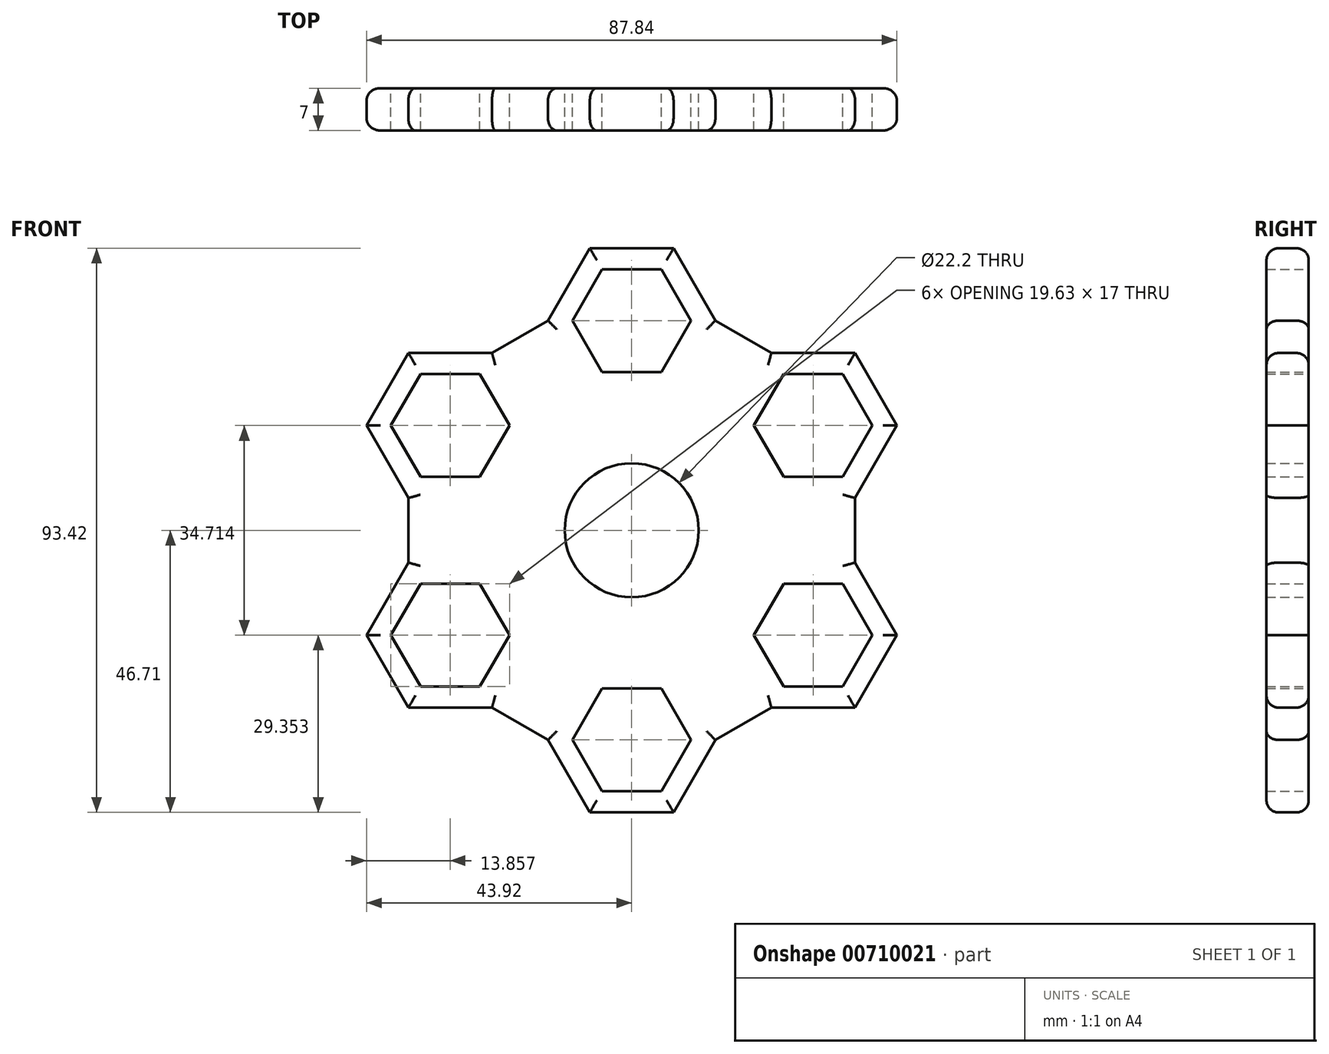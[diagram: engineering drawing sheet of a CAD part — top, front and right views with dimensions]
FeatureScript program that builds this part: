
annotation { "Feature Type Name" : "Feature", "Feature Type Description" : "" }
export const myFeature = defineFeature(function(context is Context, id is Id, definition is map)
    precondition{}
    {
        {
            var Q0;
            Q0=qCreatedBy(makeId("Front.planeOp"),FACE);
            var sketch = newSketch(context, id + "F0", { "sketchPlane" : qUnion([Q0])});
            skCircle(sketch, "E0", {"center": v(0, 0) * mm, "radius": 14.5 * mm});
            skCircle(sketch, "E1", {"center": v(0, 0) * mm, "radius": 11.1 * mm});
            skCircle(sketch, "E2.cCircle", {"center": v(0, 34.71) * mm, "radius": 8.5 * mm, "construction": true});
            skLineSegment(sketch, "E2.0", {"start": v(4.9, 26.21) * mm, "end": v(-4.9, 26.21) * mm});
            skLineSegment(sketch, "E2.1", {"start": v(-4.9, 26.21) * mm, "end": v(-9.81, 34.71) * mm});
            skLineSegment(sketch, "E2.2", {"start": v(-9.81, 34.71) * mm, "end": v(-4.9, 43.21) * mm});
            skLineSegment(sketch, "E2.3", {"start": v(-4.9, 43.21) * mm, "end": v(4.9, 43.21) * mm});
            skLineSegment(sketch, "E2.4", {"start": v(4.9, 43.21) * mm, "end": v(9.81, 34.71) * mm});
            skLineSegment(sketch, "E2.5", {"start": v(9.81, 34.71) * mm, "end": v(4.9, 26.21) * mm});
            skPoint(sketch, "E2.0.midPoint", {"position": v(0, 26.21) * mm});
            skCircle(sketch, "E3.cCircle", {"center": v(0, 34.71) * mm, "radius": 12 * mm, "construction": true});
            skLineSegment(sketch, "E3.0", {"start": v(6.93, 22.71) * mm, "end": v(-6.93, 22.71) * mm});
            skLineSegment(sketch, "E3.1", {"start": v(-6.93, 22.71) * mm, "end": v(-13.86, 34.71) * mm});
            skLineSegment(sketch, "E3.2", {"start": v(-13.86, 34.71) * mm, "end": v(-6.93, 46.71) * mm});
            skLineSegment(sketch, "E3.3", {"start": v(-6.93, 46.71) * mm, "end": v(6.93, 46.71) * mm});
            skLineSegment(sketch, "E3.4", {"start": v(6.93, 46.71) * mm, "end": v(13.86, 34.71) * mm});
            skLineSegment(sketch, "E3.5", {"start": v(13.86, 34.71) * mm, "end": v(6.93, 22.71) * mm});
            skPoint(sketch, "E3.0.midPoint", {"position": v(0, 22.71) * mm});
            skCircle(sketch, "E4.1.1", {"center": v(-30.06, 17.36) * mm, "radius": 12 * mm, "construction": true});
            skLineSegment(sketch, "E4.1.2", {"start": v(-23.14, 5.36) * mm, "end": v(-37, 5.36) * mm});
            skLineSegment(sketch, "E4.1.3", {"start": v(-37, 5.36) * mm, "end": v(-43.92, 17.36) * mm});
            skPoint(sketch, "E4.1.4", {"position": v(-22.7, 13.1) * mm});
            skLineSegment(sketch, "E4.1.6", {"start": v(-23.14, 29.36) * mm, "end": v(-16.2, 17.36) * mm});
            skLineSegment(sketch, "E4.1.7", {"start": v(-37, 29.36) * mm, "end": v(-23.14, 29.36) * mm});
            skLineSegment(sketch, "E4.1.8", {"start": v(-43.92, 17.36) * mm, "end": v(-37, 29.36) * mm});
            skPoint(sketch, "E4.1.9", {"position": v(-19.67, 11.36) * mm});
            skCircle(sketch, "E4.1.10", {"center": v(-30.06, 17.36) * mm, "radius": 8.5 * mm, "construction": true});
            skLineSegment(sketch, "E4.1.11", {"start": v(-16.2, 17.36) * mm, "end": v(-23.14, 5.36) * mm});
            skLineSegment(sketch, "E4.1.12", {"start": v(-25.16, 25.86) * mm, "end": v(-20.25, 17.36) * mm});
            skLineSegment(sketch, "E4.1.13", {"start": v(-34.97, 25.86) * mm, "end": v(-25.16, 25.86) * mm});
            skLineSegment(sketch, "E4.1.14", {"start": v(-39.88, 17.36) * mm, "end": v(-34.97, 25.86) * mm});
            skLineSegment(sketch, "E4.1.15", {"start": v(-20.25, 17.36) * mm, "end": v(-25.16, 8.86) * mm});
            skLineSegment(sketch, "E4.1.16", {"start": v(-25.16, 8.86) * mm, "end": v(-34.97, 8.86) * mm});
            skLineSegment(sketch, "E4.1.17", {"start": v(-34.97, 8.86) * mm, "end": v(-39.88, 17.36) * mm});
            skCircle(sketch, "E4.2.1", {"center": v(-30.06, -17.36) * mm, "radius": 12 * mm, "construction": true});
            skLineSegment(sketch, "E4.2.2", {"start": v(-16.2, -17.36) * mm, "end": v(-23.14, -29.36) * mm});
            skLineSegment(sketch, "E4.2.3", {"start": v(-23.14, -29.36) * mm, "end": v(-37, -29.36) * mm});
            skPoint(sketch, "E4.2.4", {"position": v(-22.7, -13.1) * mm});
            skLineSegment(sketch, "E4.2.6", {"start": v(-37, -5.36) * mm, "end": v(-23.14, -5.36) * mm});
            skLineSegment(sketch, "E4.2.7", {"start": v(-43.92, -17.36) * mm, "end": v(-37, -5.36) * mm});
            skLineSegment(sketch, "E4.2.8", {"start": v(-37, -29.36) * mm, "end": v(-43.92, -17.36) * mm});
            skPoint(sketch, "E4.2.9", {"position": v(-19.67, -11.36) * mm});
            skCircle(sketch, "E4.2.10", {"center": v(-30.06, -17.36) * mm, "radius": 8.5 * mm, "construction": true});
            skLineSegment(sketch, "E4.2.11", {"start": v(-23.14, -5.36) * mm, "end": v(-16.2, -17.36) * mm});
            skLineSegment(sketch, "E4.2.12", {"start": v(-34.97, -8.86) * mm, "end": v(-25.16, -8.86) * mm});
            skLineSegment(sketch, "E4.2.13", {"start": v(-39.88, -17.36) * mm, "end": v(-34.97, -8.86) * mm});
            skLineSegment(sketch, "E4.2.14", {"start": v(-34.97, -25.86) * mm, "end": v(-39.88, -17.36) * mm});
            skLineSegment(sketch, "E4.2.15", {"start": v(-25.16, -8.86) * mm, "end": v(-20.25, -17.36) * mm});
            skLineSegment(sketch, "E4.2.16", {"start": v(-20.25, -17.36) * mm, "end": v(-25.16, -25.86) * mm});
            skLineSegment(sketch, "E4.2.17", {"start": v(-25.16, -25.86) * mm, "end": v(-34.97, -25.86) * mm});
            skCircle(sketch, "E4.3.1", {"center": v(0, -34.71) * mm, "radius": 12 * mm, "construction": true});
            skLineSegment(sketch, "E4.3.2", {"start": v(6.93, -22.71) * mm, "end": v(13.86, -34.71) * mm});
            skLineSegment(sketch, "E4.3.3", {"start": v(13.86, -34.71) * mm, "end": v(6.93, -46.71) * mm});
            skPoint(sketch, "E4.3.4", {"position": v(0, -26.21) * mm});
            skLineSegment(sketch, "E4.3.6", {"start": v(-13.86, -34.71) * mm, "end": v(-6.93, -22.71) * mm});
            skLineSegment(sketch, "E4.3.7", {"start": v(-6.93, -46.71) * mm, "end": v(-13.86, -34.71) * mm});
            skLineSegment(sketch, "E4.3.8", {"start": v(6.93, -46.71) * mm, "end": v(-6.93, -46.71) * mm});
            skPoint(sketch, "E4.3.9", {"position": v(0, -22.71) * mm});
            skCircle(sketch, "E4.3.10", {"center": v(0, -34.71) * mm, "radius": 8.5 * mm, "construction": true});
            skLineSegment(sketch, "E4.3.11", {"start": v(-6.93, -22.71) * mm, "end": v(6.93, -22.71) * mm});
            skLineSegment(sketch, "E4.3.12", {"start": v(-9.81, -34.71) * mm, "end": v(-4.9, -26.21) * mm});
            skLineSegment(sketch, "E4.3.13", {"start": v(-4.9, -43.21) * mm, "end": v(-9.81, -34.71) * mm});
            skLineSegment(sketch, "E4.3.14", {"start": v(4.9, -43.21) * mm, "end": v(-4.9, -43.21) * mm});
            skLineSegment(sketch, "E4.3.15", {"start": v(-4.9, -26.21) * mm, "end": v(4.9, -26.21) * mm});
            skLineSegment(sketch, "E4.3.16", {"start": v(4.9, -26.21) * mm, "end": v(9.81, -34.71) * mm});
            skLineSegment(sketch, "E4.3.17", {"start": v(9.81, -34.71) * mm, "end": v(4.9, -43.21) * mm});
            skCircle(sketch, "E4.4.1", {"center": v(30.06, -17.36) * mm, "radius": 12 * mm, "construction": true});
            skLineSegment(sketch, "E4.4.2", {"start": v(23.14, -5.36) * mm, "end": v(37, -5.36) * mm});
            skLineSegment(sketch, "E4.4.3", {"start": v(37, -5.36) * mm, "end": v(43.92, -17.36) * mm});
            skPoint(sketch, "E4.4.4", {"position": v(22.7, -13.1) * mm});
            skLineSegment(sketch, "E4.4.6", {"start": v(23.14, -29.36) * mm, "end": v(16.2, -17.36) * mm});
            skLineSegment(sketch, "E4.4.7", {"start": v(37, -29.36) * mm, "end": v(23.14, -29.36) * mm});
            skLineSegment(sketch, "E4.4.8", {"start": v(43.92, -17.36) * mm, "end": v(37, -29.36) * mm});
            skPoint(sketch, "E4.4.9", {"position": v(19.67, -11.36) * mm});
            skCircle(sketch, "E4.4.10", {"center": v(30.06, -17.36) * mm, "radius": 8.5 * mm, "construction": true});
            skLineSegment(sketch, "E4.4.11", {"start": v(16.2, -17.36) * mm, "end": v(23.14, -5.36) * mm});
            skLineSegment(sketch, "E4.4.12", {"start": v(25.16, -25.86) * mm, "end": v(20.25, -17.36) * mm});
            skLineSegment(sketch, "E4.4.13", {"start": v(34.97, -25.86) * mm, "end": v(25.16, -25.86) * mm});
            skLineSegment(sketch, "E4.4.14", {"start": v(39.88, -17.36) * mm, "end": v(34.97, -25.86) * mm});
            skLineSegment(sketch, "E4.4.15", {"start": v(20.25, -17.36) * mm, "end": v(25.16, -8.86) * mm});
            skLineSegment(sketch, "E4.4.16", {"start": v(25.16, -8.86) * mm, "end": v(34.97, -8.86) * mm});
            skLineSegment(sketch, "E4.4.17", {"start": v(34.97, -8.86) * mm, "end": v(39.88, -17.36) * mm});
            skCircle(sketch, "E4.5.1", {"center": v(30.06, 17.36) * mm, "radius": 12 * mm, "construction": true});
            skLineSegment(sketch, "E4.5.2", {"start": v(16.2, 17.36) * mm, "end": v(23.14, 29.36) * mm});
            skLineSegment(sketch, "E4.5.3", {"start": v(23.14, 29.36) * mm, "end": v(37, 29.36) * mm});
            skPoint(sketch, "E4.5.4", {"position": v(22.7, 13.1) * mm});
            skLineSegment(sketch, "E4.5.6", {"start": v(37, 5.36) * mm, "end": v(23.14, 5.36) * mm});
            skLineSegment(sketch, "E4.5.7", {"start": v(43.92, 17.36) * mm, "end": v(37, 5.36) * mm});
            skLineSegment(sketch, "E4.5.8", {"start": v(37, 29.36) * mm, "end": v(43.92, 17.36) * mm});
            skPoint(sketch, "E4.5.9", {"position": v(19.67, 11.36) * mm});
            skCircle(sketch, "E4.5.10", {"center": v(30.06, 17.36) * mm, "radius": 8.5 * mm, "construction": true});
            skLineSegment(sketch, "E4.5.11", {"start": v(23.14, 5.36) * mm, "end": v(16.2, 17.36) * mm});
            skLineSegment(sketch, "E4.5.12", {"start": v(34.97, 8.86) * mm, "end": v(25.16, 8.86) * mm});
            skLineSegment(sketch, "E4.5.13", {"start": v(39.88, 17.36) * mm, "end": v(34.97, 8.86) * mm});
            skLineSegment(sketch, "E4.5.14", {"start": v(34.97, 25.86) * mm, "end": v(39.88, 17.36) * mm});
            skLineSegment(sketch, "E4.5.15", {"start": v(25.16, 8.86) * mm, "end": v(20.25, 17.36) * mm});
            skLineSegment(sketch, "E4.5.16", {"start": v(20.25, 17.36) * mm, "end": v(25.16, 25.86) * mm});
            skLineSegment(sketch, "E4.5.17", {"start": v(25.16, 25.86) * mm, "end": v(34.97, 25.86) * mm});
            skLineSegment(sketch, "E5", {"start": v(13.86, 34.71) * mm, "end": v(23.14, 29.36) * mm});
            skLineSegment(sketch, "E6.1.0", {"start": v(-23.14, 29.36) * mm, "end": v(-13.86, 34.71) * mm});
            skLineSegment(sketch, "E6.2.0", {"start": v(-37, -5.36) * mm, "end": v(-37, 5.36) * mm});
            skLineSegment(sketch, "E6.3.0", {"start": v(-13.86, -34.71) * mm, "end": v(-23.14, -29.36) * mm});
            skLineSegment(sketch, "E6.4.0", {"start": v(23.14, -29.36) * mm, "end": v(13.86, -34.71) * mm});
            skLineSegment(sketch, "E6.5.0", {"start": v(37, 5.36) * mm, "end": v(37, -5.36) * mm});
            skSolve(sketch);
        }
        {
            var Q0;
            Q0=makeQuery(id+"F0.imprint","IMPRINT",FACE,{"disambiguationData":[TD([[makeQuery(id+"F0.imprint","IMPRINT",EDGE,{"derivedFrom":sQuery(id+"F0.wireOp",EDGE,"E4.1.2")}),-1.0]])]});
            var Q1;
            Q1=makeQuery(id+"F0.imprint","IMPRINT",FACE,{"disambiguationData":[TD([[makeQuery(id+"F0.imprint","IMPRINT",EDGE,{"derivedFrom":sQuery(id+"F0.wireOp",EDGE,"E2.0")}),1.0]])]});
            var Q2;
            Q2=makeQuery(id+"F0.imprint","IMPRINT",FACE,{"disambiguationData":[TD([[makeQuery(id+"F0.imprint","IMPRINT",EDGE,{"derivedFrom":sQuery(id+"F0.wireOp",EDGE,"E3.0")}),1.0]])]});
            var Q3;
            Q3=makeQuery(id+"F0.imprint","IMPRINT",FACE,{"disambiguationData":[TD([[makeQuery(id+"F0.imprint","IMPRINT",EDGE,{"derivedFrom":sQuery(id+"F0.wireOp",EDGE,"E1")}),-1.0]])]});
            var Q4;
            Q4=makeQuery(id+"F0.imprint","IMPRINT",FACE,{"disambiguationData":[TD([[makeQuery(id+"F0.imprint","IMPRINT",EDGE,{"derivedFrom":sQuery(id+"F0.wireOp",EDGE,"E4.2.2")}),-1.0]])]});
            var Q5;
            Q5=makeQuery(id+"F0.imprint","IMPRINT",FACE,{"disambiguationData":[TD([[makeQuery(id+"F0.imprint","IMPRINT",EDGE,{"derivedFrom":sQuery(id+"F0.wireOp",EDGE,"E4.3.2")}),-1.0]])]});
            var Q6;
            Q6=makeQuery(id+"F0.imprint","IMPRINT",FACE,{"disambiguationData":[TD([[makeQuery(id+"F0.imprint","IMPRINT",EDGE,{"derivedFrom":sQuery(id+"F0.wireOp",EDGE,"E4.4.2")}),-1.0]])]});
            var Q7;
            Q7=makeQuery(id+"F0.imprint","IMPRINT",FACE,{"disambiguationData":[TD([[makeQuery(id+"F0.imprint","IMPRINT",EDGE,{"derivedFrom":sQuery(id+"F0.wireOp",EDGE,"E4.5.2")}),-1.0]])]});
            extrude(context, id + "F1", {"entities" : qUnion([Q0, Q1, Q2, Q3, Q4, Q5, Q6, Q7]), "depth" : 7 * mm, "offsetDistance" : 25 * mm});
        }
        {
            var Q0;
            Q0=makeQuery(id+"F1.opExtrude","CAP_EDGE",EDGE,{"disambiguationData":[OSD([sQuery(id+"F0.wireOp",EDGE,"E3.3")])],"isStart":false});
            var Q1;
            Q1=makeQuery(id+"F1.opExtrude","CAP_EDGE",EDGE,{"disambiguationData":[OSD([sQuery(id+"F0.wireOp",EDGE,"E3.4")])],"isStart":false});
            var Q2;
            Q2=makeQuery(id+"F1.opExtrude","CAP_EDGE",EDGE,{"disambiguationData":[OSD([sQuery(id+"F0.wireOp",EDGE,"E5")])],"isStart":false});
            var Q3;
            Q3=makeQuery(id+"F1.opExtrude","CAP_EDGE",EDGE,{"disambiguationData":[OSD([sQuery(id+"F0.wireOp",EDGE,"E4.5.3")])],"isStart":false});
            var Q4;
            Q4=makeQuery(id+"F1.opExtrude","CAP_EDGE",EDGE,{"disambiguationData":[OSD([sQuery(id+"F0.wireOp",EDGE,"E4.5.8")])],"isStart":false});
            var Q5;
            Q5=makeQuery(id+"F1.opExtrude","CAP_EDGE",EDGE,{"disambiguationData":[OSD([sQuery(id+"F0.wireOp",EDGE,"E4.5.7")])],"isStart":false});
            var Q6;
            Q6=makeQuery(id+"F1.opExtrude","CAP_EDGE",EDGE,{"disambiguationData":[OSD([sQuery(id+"F0.wireOp",EDGE,"E6.5.0")])],"isStart":false});
            var Q7;
            Q7=makeQuery(id+"F1.opExtrude","CAP_EDGE",EDGE,{"disambiguationData":[OSD([sQuery(id+"F0.wireOp",EDGE,"E4.4.3")])],"isStart":false});
            var Q8;
            Q8=makeQuery(id+"F1.opExtrude","CAP_EDGE",EDGE,{"disambiguationData":[OSD([sQuery(id+"F0.wireOp",EDGE,"E4.4.8")])],"isStart":false});
            var Q9;
            Q9=makeQuery(id+"F1.opExtrude","CAP_EDGE",EDGE,{"disambiguationData":[OSD([sQuery(id+"F0.wireOp",EDGE,"E3.2")])],"isStart":false});
            var Q10;
            Q10=makeQuery(id+"F1.opExtrude","CAP_EDGE",EDGE,{"disambiguationData":[OSD([sQuery(id+"F0.wireOp",EDGE,"E6.1.0")])],"isStart":false});
            var Q11;
            Q11=makeQuery(id+"F1.opExtrude","CAP_EDGE",EDGE,{"disambiguationData":[OSD([sQuery(id+"F0.wireOp",EDGE,"E4.1.7")])],"isStart":false});
            var Q12;
            Q12=makeQuery(id+"F1.opExtrude","CAP_EDGE",EDGE,{"disambiguationData":[OSD([sQuery(id+"F0.wireOp",EDGE,"E4.1.8")])],"isStart":false});
            var Q13;
            Q13=makeQuery(id+"F1.opExtrude","CAP_EDGE",EDGE,{"disambiguationData":[OSD([sQuery(id+"F0.wireOp",EDGE,"E4.1.3")])],"isStart":false});
            var Q14;
            Q14=makeQuery(id+"F1.opExtrude","CAP_EDGE",EDGE,{"disambiguationData":[OSD([sQuery(id+"F0.wireOp",EDGE,"E6.2.0")])],"isStart":false});
            var Q15;
            Q15=makeQuery(id+"F1.opExtrude","CAP_EDGE",EDGE,{"disambiguationData":[OSD([sQuery(id+"F0.wireOp",EDGE,"E4.2.7")])],"isStart":false});
            var Q16;
            Q16=makeQuery(id+"F1.opExtrude","CAP_EDGE",EDGE,{"disambiguationData":[OSD([sQuery(id+"F0.wireOp",EDGE,"E4.2.8")])],"isStart":false});
            var Q17;
            Q17=makeQuery(id+"F1.opExtrude","CAP_EDGE",EDGE,{"disambiguationData":[OSD([sQuery(id+"F0.wireOp",EDGE,"E6.3.0")])],"isStart":false});
            var Q18;
            Q18=makeQuery(id+"F1.opExtrude","CAP_EDGE",EDGE,{"disambiguationData":[OSD([sQuery(id+"F0.wireOp",EDGE,"E4.3.7")])],"isStart":false});
            var Q19;
            Q19=makeQuery(id+"F1.opExtrude","CAP_EDGE",EDGE,{"disambiguationData":[OSD([sQuery(id+"F0.wireOp",EDGE,"E4.3.8")])],"isStart":false});
            var Q20;
            Q20=makeQuery(id+"F1.opExtrude","CAP_EDGE",EDGE,{"disambiguationData":[OSD([sQuery(id+"F0.wireOp",EDGE,"E4.3.3")])],"isStart":false});
            var Q21;
            Q21=makeQuery(id+"F1.opExtrude","CAP_EDGE",EDGE,{"disambiguationData":[OSD([sQuery(id+"F0.wireOp",EDGE,"E6.4.0")])],"isStart":false});
            var Q22;
            Q22=makeQuery(id+"F1.opExtrude","CAP_EDGE",EDGE,{"disambiguationData":[OSD([sQuery(id+"F0.wireOp",EDGE,"E4.4.7")])],"isStart":false});
            var Q23;
            Q23=makeQuery(id+"F1.opExtrude","CAP_EDGE",EDGE,{"disambiguationData":[OSD([sQuery(id+"F0.wireOp",EDGE,"E4.2.3")])],"isStart":false});
            var Q24;
            Q24=makeQuery(id+"F1.opExtrude","CAP_EDGE",EDGE,{"disambiguationData":[OSD([sQuery(id+"F0.wireOp",EDGE,"E4.3.8")])],"isStart":true});
            var Q25;
            Q25=makeQuery(id+"F1.opExtrude","CAP_EDGE",EDGE,{"disambiguationData":[OSD([sQuery(id+"F0.wireOp",EDGE,"E4.3.3")])],"isStart":true});
            var Q26;
            Q26=makeQuery(id+"F1.opExtrude","CAP_EDGE",EDGE,{"disambiguationData":[OSD([sQuery(id+"F0.wireOp",EDGE,"E6.4.0")])],"isStart":true});
            var Q27;
            Q27=makeQuery(id+"F1.opExtrude","CAP_EDGE",EDGE,{"disambiguationData":[OSD([sQuery(id+"F0.wireOp",EDGE,"E4.4.7")])],"isStart":true});
            var Q28;
            Q28=makeQuery(id+"F1.opExtrude","CAP_EDGE",EDGE,{"disambiguationData":[OSD([sQuery(id+"F0.wireOp",EDGE,"E4.4.8")])],"isStart":true});
            var Q29;
            Q29=makeQuery(id+"F1.opExtrude","CAP_EDGE",EDGE,{"disambiguationData":[OSD([sQuery(id+"F0.wireOp",EDGE,"E4.4.3")])],"isStart":true});
            var Q30;
            Q30=makeQuery(id+"F1.opExtrude","CAP_EDGE",EDGE,{"disambiguationData":[OSD([sQuery(id+"F0.wireOp",EDGE,"E6.5.0")])],"isStart":true});
            var Q31;
            Q31=makeQuery(id+"F1.opExtrude","CAP_EDGE",EDGE,{"disambiguationData":[OSD([sQuery(id+"F0.wireOp",EDGE,"E4.5.7")])],"isStart":true});
            var Q32;
            Q32=makeQuery(id+"F1.opExtrude","CAP_EDGE",EDGE,{"disambiguationData":[OSD([sQuery(id+"F0.wireOp",EDGE,"E4.5.8")])],"isStart":true});
            var Q33;
            Q33=makeQuery(id+"F1.opExtrude","CAP_EDGE",EDGE,{"disambiguationData":[OSD([sQuery(id+"F0.wireOp",EDGE,"E4.5.3")])],"isStart":true});
            var Q34;
            Q34=makeQuery(id+"F1.opExtrude","CAP_EDGE",EDGE,{"disambiguationData":[OSD([sQuery(id+"F0.wireOp",EDGE,"E5")])],"isStart":true});
            var Q35;
            Q35=makeQuery(id+"F1.opExtrude","CAP_EDGE",EDGE,{"disambiguationData":[OSD([sQuery(id+"F0.wireOp",EDGE,"E3.4")])],"isStart":true});
            var Q36;
            Q36=makeQuery(id+"F1.opExtrude","CAP_EDGE",EDGE,{"disambiguationData":[OSD([sQuery(id+"F0.wireOp",EDGE,"E3.3")])],"isStart":true});
            var Q37;
            Q37=makeQuery(id+"F1.opExtrude","CAP_EDGE",EDGE,{"disambiguationData":[OSD([sQuery(id+"F0.wireOp",EDGE,"E3.2")])],"isStart":true});
            var Q38;
            Q38=makeQuery(id+"F1.opExtrude","CAP_EDGE",EDGE,{"disambiguationData":[OSD([sQuery(id+"F0.wireOp",EDGE,"E6.1.0")])],"isStart":true});
            var Q39;
            Q39=makeQuery(id+"F1.opExtrude","CAP_EDGE",EDGE,{"disambiguationData":[OSD([sQuery(id+"F0.wireOp",EDGE,"E4.1.7")])],"isStart":true});
            var Q40;
            Q40=makeQuery(id+"F1.opExtrude","CAP_EDGE",EDGE,{"disambiguationData":[OSD([sQuery(id+"F0.wireOp",EDGE,"E4.1.8")])],"isStart":true});
            var Q41;
            Q41=makeQuery(id+"F1.opExtrude","CAP_EDGE",EDGE,{"disambiguationData":[OSD([sQuery(id+"F0.wireOp",EDGE,"E4.1.3")])],"isStart":true});
            var Q42;
            Q42=makeQuery(id+"F1.opExtrude","CAP_EDGE",EDGE,{"disambiguationData":[OSD([sQuery(id+"F0.wireOp",EDGE,"E6.2.0")])],"isStart":true});
            var Q43;
            Q43=makeQuery(id+"F1.opExtrude","CAP_EDGE",EDGE,{"disambiguationData":[OSD([sQuery(id+"F0.wireOp",EDGE,"E4.2.7")])],"isStart":true});
            var Q44;
            Q44=makeQuery(id+"F1.opExtrude","CAP_EDGE",EDGE,{"disambiguationData":[OSD([sQuery(id+"F0.wireOp",EDGE,"E4.2.8")])],"isStart":true});
            var Q45;
            Q45=makeQuery(id+"F1.opExtrude","CAP_EDGE",EDGE,{"disambiguationData":[OSD([sQuery(id+"F0.wireOp",EDGE,"E4.2.3")])],"isStart":true});
            var Q46;
            Q46=makeQuery(id+"F1.opExtrude","CAP_EDGE",EDGE,{"disambiguationData":[OSD([sQuery(id+"F0.wireOp",EDGE,"E6.3.0")])],"isStart":true});
            var Q47;
            Q47=makeQuery(id+"F1.opExtrude","CAP_EDGE",EDGE,{"disambiguationData":[OSD([sQuery(id+"F0.wireOp",EDGE,"E4.3.7")])],"isStart":true});
            fillet(context, id + "F2", {"entities" : qUnion([Q0, Q1, Q2, Q3, Q4, Q5, Q6, Q7, Q8, Q9, Q10, Q11, Q12, Q13, Q14, Q15, Q16, Q17, Q18, Q19, Q20, Q21, Q22, Q23, Q24, Q25, Q26, Q27, Q28, Q29, Q30, Q31, Q32, Q33, Q34, Q35, Q36, Q37, Q38, Q39, Q40, Q41, Q42, Q43, Q44, Q45, Q46, Q47]), "radius" : 2 * mm, "tangentPropagation" : true, "allowEdgeOverflow" : false});
        }
    });
